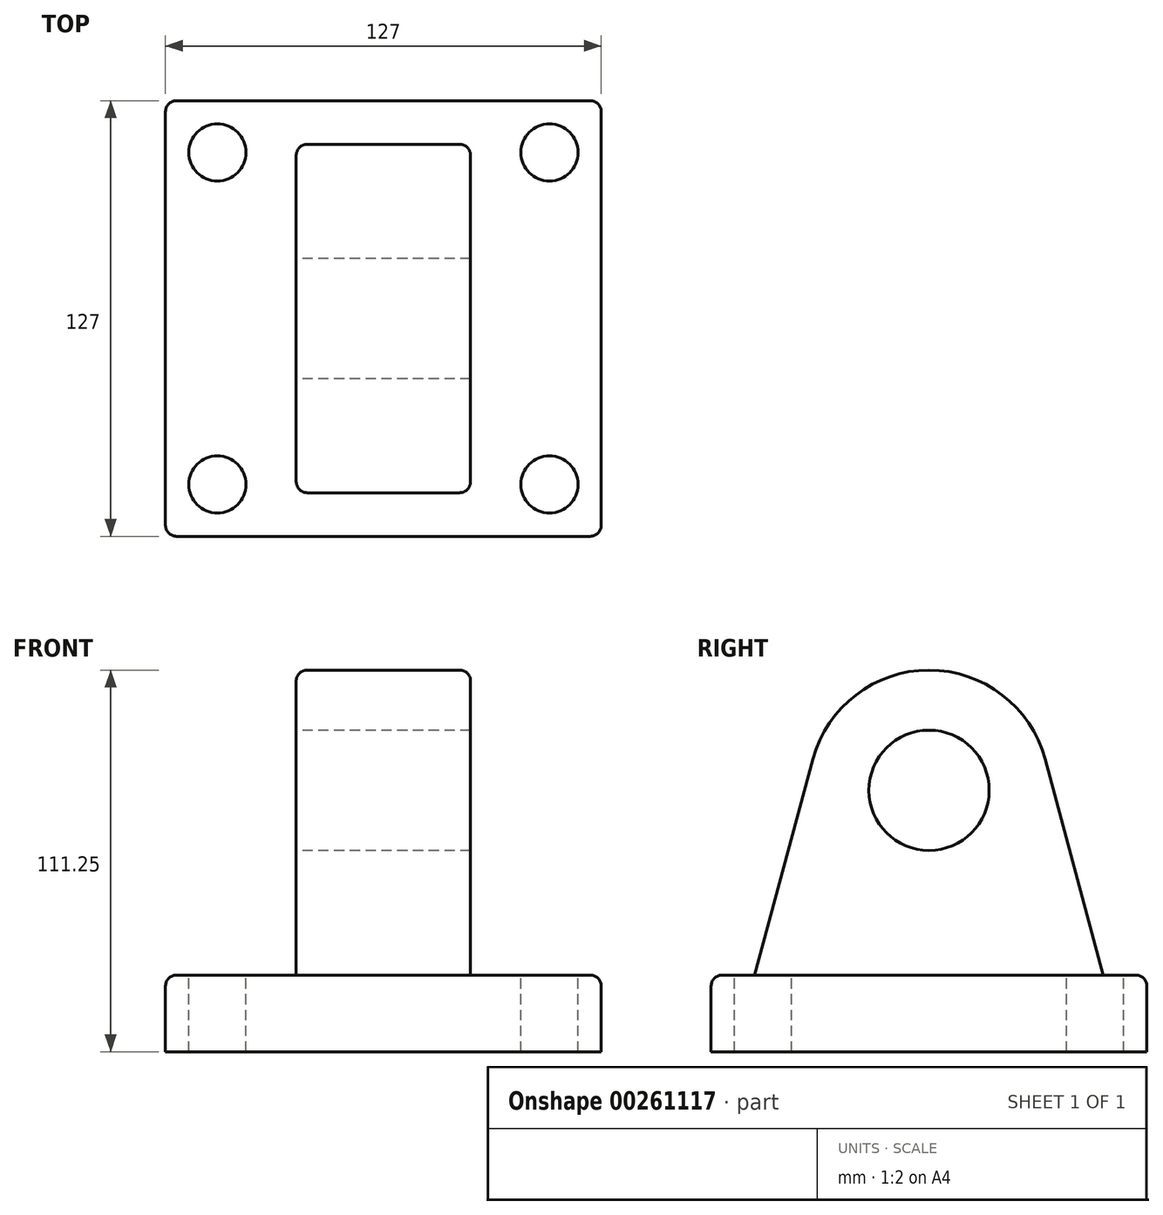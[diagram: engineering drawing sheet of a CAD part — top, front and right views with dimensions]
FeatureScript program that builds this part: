
annotation { "Feature Type Name" : "Feature", "Feature Type Description" : "" }
export const myFeature = defineFeature(function(context is Context, id is Id, definition is map)
    precondition{}
    {
        {
            var Q0;
            Q0=qCreatedBy(makeId("Top.planeOp"),FACE);
            var sketch = newSketch(context, id + "F0", { "sketchPlane" : qUnion([Q0])});
            skLineSegment(sketch, "E0.bottom", {"start": v(-63.5, -63.5) * mm, "end": v(63.5, -63.5) * mm});
            skLineSegment(sketch, "E0.top", {"start": v(-63.5, 63.5) * mm, "end": v(63.5, 63.5) * mm});
            skLineSegment(sketch, "E0.left", {"start": v(-63.5, -63.5) * mm, "end": v(-63.5, 63.5) * mm});
            skLineSegment(sketch, "E0.right", {"start": v(63.5, -63.5) * mm, "end": v(63.5, 63.5) * mm});
            skPoint(sketch, "E0.middle", {"position": v(0, 0) * mm});
            skCircle(sketch, "E1", {"center": v(-48.39, -48.39) * mm, "radius": 8.33 * mm});
            skCircle(sketch, "E2.0.1.0", {"center": v(-48.39, 48.39) * mm, "radius": 8.33 * mm});
            skCircle(sketch, "E2.1.0.0", {"center": v(48.39, -48.39) * mm, "radius": 8.33 * mm});
            skCircle(sketch, "E2.1.1.0", {"center": v(48.39, 48.39) * mm, "radius": 8.33 * mm});
            skLineSegment(sketch, "E2.direction1", {"start": v(-48.39, -48.39) * mm, "end": v(48.39, -48.39) * mm, "construction": true});
            skLineSegment(sketch, "E2.direction2", {"start": v(-48.39, -48.39) * mm, "end": v(-48.39, 48.39) * mm, "construction": true});
            skSolve(sketch);
        }
        {
            var Q0;
            Q0=makeQuery(id+"F0.imprint","IMPRINT",FACE,{"disambiguationData":[TD([[makeQuery(id+"F0.imprint","IMPRINT",EDGE,{"derivedFrom":sQuery(id+"F0.wireOp",EDGE,"E0.bottom")}),1.0]])]});
            extrude(context, id + "F1", {"entities" : qUnion([Q0]), "oppositeDirection" : true, "depth" : 22.35 * mm});
        }
        {
            var Q0;
            Q0=qCreatedBy(makeId("Right.planeOp"),FACE);
            var sketch = newSketch(context, id + "F2", { "sketchPlane" : qUnion([Q0])});
            skCircle(sketch, "E3", {"center": v(0, 53.85) * mm, "radius": 17.53 * mm});
            skArc(sketch, "E4", {"start": v(33.85, 62.96) * mm, "mid": v(0, 88.9) * mm, "end": v(-33.85, 62.96) * mm});
            skLineSegment(sketch, "E5", {"start": v(-50.8, 0) * mm, "end": v(-33.85, 62.96) * mm});
            skLineSegment(sketch, "E6.MirrorCS", {"start": v(50.8, 0) * mm, "end": v(33.85, 62.96) * mm});
            skLineSegment(sketch, "E7", {"start": v(-50.8, 0) * mm, "end": v(50.8, 0) * mm});
            skSolve(sketch);
        }
        {
            var Q0;
            Q0 = qSketchRegion(id + "F2", true);
            extrude(context, id + "F3", {"entities" : qUnion([Q0]), "operationType" : NewBodyOperationType.ADD, "endBound" : BoundingType.SYMMETRIC, "depth" : 50.8 * mm});
        }
        {
            var Q0;
            Q0=makeQuery(id+"F3.opExtrude","CAP_EDGE",EDGE,{"disambiguationData":[OSD([sQuery(id+"F2.wireOp",EDGE,"E7")])],"isStart":false});
            var Q1;
            Q1=makeQuery(id+"F3.opExtrude","SWEPT_EDGE",EDGE,{"disambiguationData":[OSD([sQuery(id+"F2.wireOp",EDGE,"E5"),sQuery(id+"F2.wireOp",EDGE,"E7")])]});
            var Q2;
            Q2=makeQuery(id+"F3.opExtrude","CAP_EDGE",EDGE,{"disambiguationData":[OSD([sQuery(id+"F2.wireOp",EDGE,"E7")])],"isStart":true});
            var Q3;
            Q3=makeQuery(id+"F3.opExtrude","SWEPT_EDGE",EDGE,{"disambiguationData":[OSD([sQuery(id+"F2.wireOp",EDGE,"E6.MirrorCS"),sQuery(id+"F2.wireOp",EDGE,"E7")])]});
            var Q4;
            Q4=makeQuery(id+"F1.opExtrude","CAP_EDGE",EDGE,{"disambiguationData":[OSD([sQuery(id+"F0.wireOp",EDGE,"E0.right")])],"isStart":true});
            var Q5;
            Q5=makeQuery(id+"F1.opExtrude","CAP_EDGE",EDGE,{"disambiguationData":[OSD([sQuery(id+"F0.wireOp",EDGE,"E0.bottom")])],"isStart":true});
            var Q6;
            Q6=makeQuery(id+"F1.opExtrude","CAP_EDGE",EDGE,{"disambiguationData":[OSD([sQuery(id+"F0.wireOp",EDGE,"E0.left")])],"isStart":true});
            var Q7;
            Q7=makeQuery(id+"F1.opExtrude","CAP_EDGE",EDGE,{"disambiguationData":[OSD([sQuery(id+"F0.wireOp",EDGE,"E0.top")])],"isStart":true});
            var Q8;
            Q8=makeQuery(id+"F3.opExtrude","CAP_EDGE",EDGE,{"disambiguationData":[OSD([sQuery(id+"F2.wireOp",EDGE,"E5")])],"isStart":false});
            var Q9;
            Q9=makeQuery(id+"F3.opExtrude","CAP_EDGE",EDGE,{"disambiguationData":[OSD([sQuery(id+"F2.wireOp",EDGE,"E5")])],"isStart":true});
            var Q10;
            Q10=makeQuery(id+"F1.opExtrude","SWEPT_EDGE",EDGE,{"disambiguationData":[OSD([sQuery(id+"F0.wireOp",EDGE,"E0.bottom"),sQuery(id+"F0.wireOp",EDGE,"E0.right")])]});
            var Q11;
            Q11=makeQuery(id+"F1.opExtrude","SWEPT_EDGE",EDGE,{"disambiguationData":[OSD([sQuery(id+"F0.wireOp",EDGE,"E0.top"),sQuery(id+"F0.wireOp",EDGE,"E0.right")])]});
            var Q12;
            Q12=makeQuery(id+"F1.opExtrude","SWEPT_EDGE",EDGE,{"disambiguationData":[OSD([sQuery(id+"F0.wireOp",EDGE,"E0.bottom"),sQuery(id+"F0.wireOp",EDGE,"E0.left")])]});
            var Q13;
            Q13=makeQuery(id+"F1.opExtrude","SWEPT_EDGE",EDGE,{"disambiguationData":[OSD([sQuery(id+"F0.wireOp",EDGE,"E0.top"),sQuery(id+"F0.wireOp",EDGE,"E0.left")])]});
            fillet(context, id + "F4", {"entities" : qUnion([Q0, Q1, Q2, Q3, Q4, Q5, Q6, Q7, Q8, Q9, Q10, Q11, Q12, Q13]), "radius" : 3.17 * mm, "tangentPropagation" : true, "allowEdgeOverflow" : false});
        }
    });
